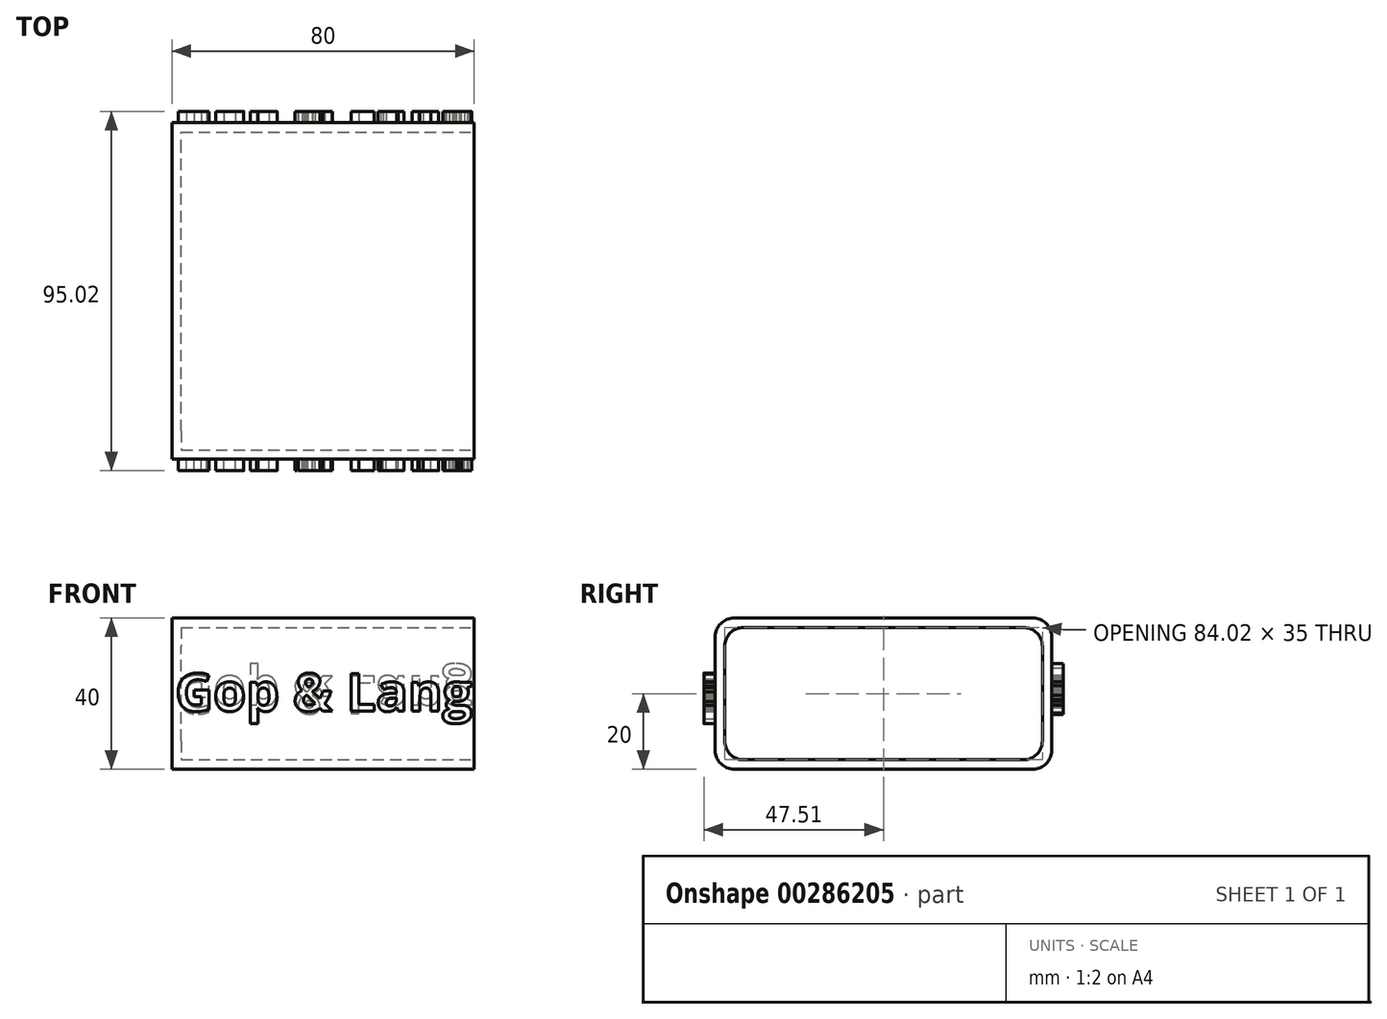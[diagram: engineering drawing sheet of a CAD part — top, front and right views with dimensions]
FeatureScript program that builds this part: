
annotation { "Feature Type Name" : "Feature", "Feature Type Description" : "" }
export const myFeature = defineFeature(function(context is Context, id is Id, definition is map)
    precondition{}
    {
        {
            var Q0;
            Q0=qCreatedBy(makeId("Top.planeOp"),FACE);
            var sketch = newSketch(context, id + "F0", { "sketchPlane" : qUnion([Q0])});
            skLineSegment(sketch, "E0.bottom", {"start": v(-40, 44.51) * mm, "end": v(40, 44.51) * mm});
            skLineSegment(sketch, "E0.top", {"start": v(-40, -44.51) * mm, "end": v(40, -44.51) * mm});
            skLineSegment(sketch, "E0.left", {"start": v(-40, 44.51) * mm, "end": v(-40, -44.51) * mm});
            skLineSegment(sketch, "E0.right", {"start": v(40, 44.51) * mm, "end": v(40, -44.51) * mm});
            skPoint(sketch, "E0.middle", {"position": v(0, 0) * mm});
            skSolve(sketch);
        }
        {
            var Q0;
            Q0=makeQuery(id+"F0.imprint","IMPRINT",FACE,{"disambiguationData":[TD([[makeQuery(id+"F0.imprint","IMPRINT",EDGE,{"derivedFrom":sQuery(id+"F0.wireOp",EDGE,"E0.bottom")}),-1.0]])]});
            extrude(context, id + "F1", {"entities" : qUnion([Q0]), "depth" : 40 * mm});
        }
        {
            var Q0;
            Q0=makeQuery(id+"F1.opExtrude","SWEPT_FACE",FACE,{"disambiguationData":[OSD([sQuery(id+"F0.wireOp",EDGE,"E0.right")])]});
            shell(context, id + "F2", {"entities" : qUnion([Q0]), "thickness" : 2.5 * mm});
        }
        {
            var Q0;
            Q0=makeQuery(id+"F1.opExtrude","CAP_EDGE",EDGE,{"disambiguationData":[OSD([sQuery(id+"F0.wireOp",EDGE,"E0.top")])],"isStart":false});
            fillet(context, id + "F3", {"entities" : qUnion([Q0]), "radius" : 5 * mm, "tangentPropagation" : true, "allowEdgeOverflow" : false});
        }
        {
            var Q0;
            Q0=makeQuery(id+"F1.opExtrude","CAP_EDGE",EDGE,{"disambiguationData":[OSD([sQuery(id+"F0.wireOp",EDGE,"E0.top")])],"isStart":true});
            fillet(context, id + "F4", {"entities" : qUnion([Q0]), "radius" : 5 * mm, "tangentPropagation" : true, "allowEdgeOverflow" : false});
        }
        {
            var Q0;
            Q0=makeQuery(id+"F1.opExtrude","CAP_EDGE",EDGE,{"disambiguationData":[OSD([sQuery(id+"F0.wireOp",EDGE,"E0.bottom")])],"isStart":true});
            var Q1;
            Q1=makeQuery(id+"F1.opExtrude","CAP_EDGE",EDGE,{"disambiguationData":[OSD([sQuery(id+"F0.wireOp",EDGE,"E0.bottom")])],"isStart":false});
            fillet(context, id + "F5", {"entities" : qUnion([Q0, Q1]), "radius" : 5 * mm, "tangentPropagation" : true, "allowEdgeOverflow" : false});
        }
        {
            var Q0;
            Q0=makeQuery(id+"F1.opExtrude","SWEPT_FACE",FACE,{"disambiguationData":[OSD([sQuery(id+"F0.wireOp",EDGE,"E0.top")])]});
            var sketch = newSketch(context, id + "F6", { "sketchPlane" : qUnion([Q0])});
            skText(sketch, "E1", { "text": "Gop & Lang", "fontName": "OpenSans-Bold.ttf"});
            const initialGuessF6  = {"E1": [-0.03913, 0.01536, 1, 0, 0.01004]};
            skSetInitialGuess(sketch, initialGuessF6);
            skSolve(sketch);
        }
        {
            var Q0;
            Q0=makeQuery(id+"F6.imprint","IMPRINT",FACE,{"disambiguationData":[TD([[makeQuery(id+"F6.imprint","IMPRINT",EDGE,{"derivedFrom":sQuery(id+"F6.wireOp",EDGE,"E1.sketch_text.stroke-37")}),-1.0]])]});
            var Q1;
            Q1=makeQuery(id+"F6.imprint","IMPRINT",FACE,{"disambiguationData":[TD([[makeQuery(id+"F6.imprint","IMPRINT",EDGE,{"derivedFrom":sQuery(id+"F6.wireOp",EDGE,"E1.sketch_text.stroke-19")}),-1.0]])]});
            var Q2;
            Q2=makeQuery(id+"F6.imprint","IMPRINT",FACE,{"disambiguationData":[TD([[makeQuery(id+"F6.imprint","IMPRINT",EDGE,{"derivedFrom":sQuery(id+"F6.wireOp",EDGE,"E1.sketch_text.stroke-0")}),-1.0]])]});
            var Q3;
            Q3=makeQuery(id+"F6.imprint","IMPRINT",FACE,{"disambiguationData":[TD([[makeQuery(id+"F6.imprint","IMPRINT",EDGE,{"derivedFrom":sQuery(id+"F6.wireOp",EDGE,"E1.sketch_text.stroke-60")}),-1.0]])]});
            var Q4;
            Q4=makeQuery(id+"F6.imprint","IMPRINT",FACE,{"disambiguationData":[TD([[makeQuery(id+"F6.imprint","IMPRINT",EDGE,{"derivedFrom":sQuery(id+"F6.wireOp",EDGE,"E1.sketch_text.stroke-94")}),-1.0]])]});
            var Q5;
            Q5=makeQuery(id+"F6.imprint","IMPRINT",FACE,{"disambiguationData":[TD([[makeQuery(id+"F6.imprint","IMPRINT",EDGE,{"derivedFrom":sQuery(id+"F6.wireOp",EDGE,"E1.sketch_text.stroke-100")}),-1.0]])]});
            var Q6;
            Q6=makeQuery(id+"F6.imprint","IMPRINT",FACE,{"disambiguationData":[TD([[makeQuery(id+"F6.imprint","IMPRINT",EDGE,{"derivedFrom":sQuery(id+"F6.wireOp",EDGE,"E1.sketch_text.stroke-125")}),-1.0]])]});
            var Q7;
            Q7=makeQuery(id+"F6.imprint","IMPRINT",FACE,{"disambiguationData":[TD([[makeQuery(id+"F6.imprint","IMPRINT",EDGE,{"derivedFrom":sQuery(id+"F6.wireOp",EDGE,"E1.sketch_text.stroke-142")}),-1.0]])]});
            extrude(context, id + "F7", {"entities" : qUnion([Q0, Q1, Q2, Q3, Q4, Q5, Q6, Q7]), "operationType" : NewBodyOperationType.ADD, "depth" : 3 * mm});
        }
        {
            var Q0;
            {var subQ0=sQuery(id+"F0.wireOp",EDGE,"E0.top");Q0=makeQuery(id+"F2.opShell","OFFSET_EDGE",EDGE,{"disambiguationData":[OSD([subQ0]),TDD([makeQuery(id+"F1.opExtrude","CAP_EDGE",EDGE,{"disambiguationData":[OSD([subQ0])],"isStart":false})])]});}
            var Q1;
            {var subQ0=sQuery(id+"F0.wireOp",EDGE,"E0.top");Q1=makeQuery(id+"F2.opShell","OFFSET_EDGE",EDGE,{"disambiguationData":[OSD([subQ0]),TDD([makeQuery(id+"F1.opExtrude","CAP_EDGE",EDGE,{"disambiguationData":[OSD([subQ0])],"isStart":true})])]});}
            fillet(context, id + "F8", {"entities" : qUnion([Q0, Q1]), "radius" : 5 * mm, "tangentPropagation" : true, "allowEdgeOverflow" : false});
        }
        {
            var Q0;
            {var subQ0=sQuery(id+"F0.wireOp",EDGE,"E0.bottom");Q0=makeQuery(id+"F2.opShell","OFFSET_EDGE",EDGE,{"disambiguationData":[OSD([subQ0]),TDD([makeQuery(id+"F1.opExtrude","CAP_EDGE",EDGE,{"disambiguationData":[OSD([subQ0])],"isStart":false})])]});}
            fillet(context, id + "F9", {"entities" : qUnion([Q0]), "radius" : 5 * mm, "tangentPropagation" : true, "allowEdgeOverflow" : false});
        }
        {
            var Q0;
            {var subQ0=sQuery(id+"F0.wireOp",EDGE,"E0.bottom");Q0=makeQuery(id+"F2.opShell","OFFSET_EDGE",EDGE,{"disambiguationData":[OSD([subQ0]),TDD([makeQuery(id+"F1.opExtrude","CAP_EDGE",EDGE,{"disambiguationData":[OSD([subQ0])],"isStart":true})])]});}
            fillet(context, id + "F10", {"entities" : qUnion([Q0]), "radius" : 5 * mm, "tangentPropagation" : true, "allowEdgeOverflow" : false});
        }
        {
            var Q0;
            Q0=makeQuery(id+"F1.opExtrude","SWEPT_FACE",FACE,{"disambiguationData":[OSD([sQuery(id+"F0.wireOp",EDGE,"E0.left")])]});
            var sketch = newSketch(context, id + "F11", { "sketchPlane" : qUnion([Q0])});
            skCircle(sketch, "E2", {"center": v(0, 20) * mm, "radius": 45 * mm, "construction": true});
            skSolve(sketch);
        }
        {
            var Q0;
            Q0=makeQuery(id+"F1.opExtrude","SWEPT_BODY",BODY,{"disambiguationData":[OSD([sQuery(id+"F0.wireOp",EDGE,"E0.bottom"),sQuery(id+"F0.wireOp",EDGE,"E0.top"),sQuery(id+"F0.wireOp",EDGE,"E0.left"),sQuery(id+"F0.wireOp",EDGE,"E0.right")])]});
            var Q1;
            Q1=sQuery(id+"F11.wireOp",EDGE,"E2");
            circularPattern(context, id + "F12", {"entities" : qUnion([Q0]), "axis" : qUnion([Q1]), "angle" : 360 * degree, "instanceCount" : 2, "oppositeDirection" : true, "equalSpace" : true});
        }
    });
